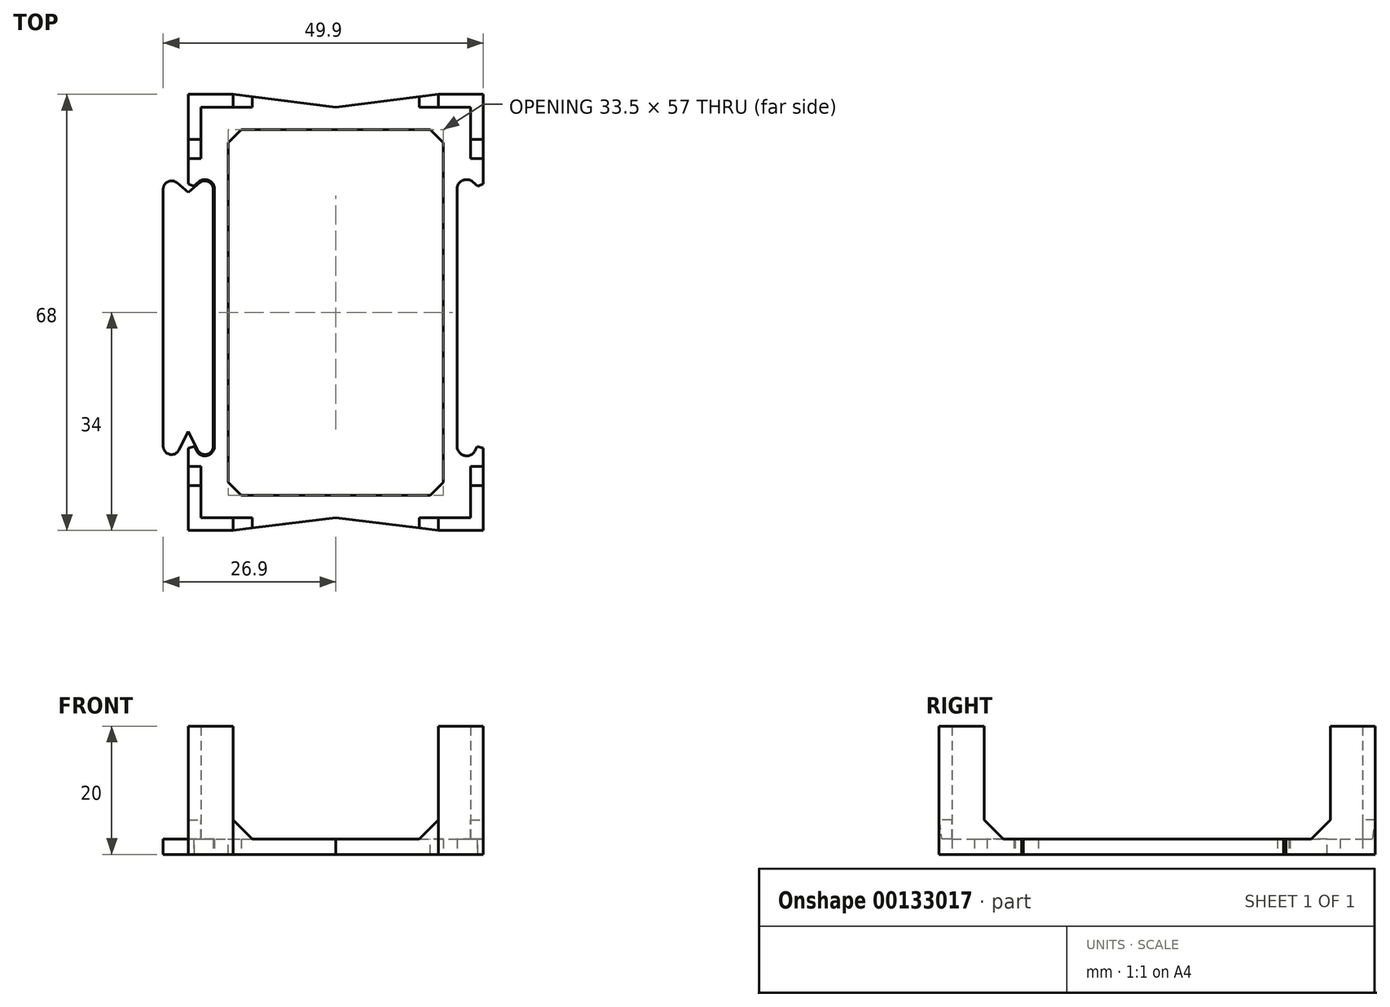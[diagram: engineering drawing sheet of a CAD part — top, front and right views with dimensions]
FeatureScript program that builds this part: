
annotation { "Feature Type Name" : "Feature", "Feature Type Description" : "" }
export const myFeature = defineFeature(function(context is Context, id is Id, definition is map)
    precondition{}
    {
        {
            var Q0;
            Q0=qCreatedBy(makeId("Top.planeOp"),FACE);
            var sketch = newSketch(context, id + "F0", { "sketchPlane" : qUnion([Q0])});
            skLineSegment(sketch, "E0.bottom", {"start": v(21, 32) * mm, "end": v(16, 32) * mm});
            skLineSegment(sketch, "E0.top", {"start": v(21, -32) * mm, "end": v(16, -32) * mm});
            skLineSegment(sketch, "E0.left", {"start": v(21, 32) * mm, "end": v(21, 27) * mm});
            skLineSegment(sketch, "E0.right", {"start": v(-21, 32) * mm, "end": v(-21, 27) * mm});
            skLineSegment(sketch, "E1", {"start": v(-16, 34) * mm, "end": v(-23, 34) * mm});
            skLineSegment(sketch, "E2", {"start": v(-23, 34) * mm, "end": v(-23, 27) * mm});
            skLineSegment(sketch, "E3", {"start": v(-16, 32) * mm, "end": v(-16, 34) * mm});
            skLineSegment(sketch, "E4", {"start": v(-21, 27) * mm, "end": v(-23, 27) * mm});
            skLineSegment(sketch, "E5", {"start": v(16, 34) * mm, "end": v(16, 32) * mm});
            skLineSegment(sketch, "E6", {"start": v(16, 34) * mm, "end": v(23, 34) * mm});
            skLineSegment(sketch, "E7", {"start": v(23, 27) * mm, "end": v(23, 34) * mm});
            skLineSegment(sketch, "E8", {"start": v(21, 27) * mm, "end": v(23, 27) * mm});
            skLineSegment(sketch, "E9", {"start": v(-23, -27) * mm, "end": v(-21, -27) * mm});
            skLineSegment(sketch, "E10", {"start": v(-23, -27) * mm, "end": v(-23, -34) * mm});
            skLineSegment(sketch, "E11", {"start": v(-16, -34) * mm, "end": v(-23, -34) * mm});
            skLineSegment(sketch, "E12", {"start": v(-16, -32) * mm, "end": v(-16, -34) * mm});
            skLineSegment(sketch, "E13", {"start": v(16, -32) * mm, "end": v(16, -34) * mm});
            skLineSegment(sketch, "E14", {"start": v(16, -34) * mm, "end": v(23, -34) * mm});
            skLineSegment(sketch, "E15", {"start": v(23, -27) * mm, "end": v(23, -34) * mm});
            skLineSegment(sketch, "E16", {"start": v(21, -27) * mm, "end": v(23, -27) * mm});
            skLineSegment(sketch, "E17", {"start": v(-16.75, 28.5) * mm, "end": v(16.75, 28.5) * mm});
            skLineSegment(sketch, "E18", {"start": v(16.75, -28.5) * mm, "end": v(-16.75, -28.5) * mm});
            skLineSegment(sketch, "E19", {"start": v(-16.75, 28.5) * mm, "end": v(-16.75, -28.5) * mm});
            skLineSegment(sketch, "E20", {"start": v(16.75, 28.5) * mm, "end": v(16.75, -28.5) * mm});
            skLineSegment(sketch, "E21", {"start": v(-16, 34) * mm, "end": v(0, 32) * mm});
            skLineSegment(sketch, "E22", {"start": v(0, 32) * mm, "end": v(16, 34) * mm});
            skLineSegment(sketch, "E23", {"start": v(-16, -34) * mm, "end": v(0, -32) * mm});
            skLineSegment(sketch, "E24", {"start": v(0, -32) * mm, "end": v(16, -34) * mm});
            skLineSegment(sketch, "E25.trimOffspring", {"start": v(21, -27) * mm, "end": v(21, -32) * mm});
            skLineSegment(sketch, "E26.trimOffspring", {"start": v(-16, -32) * mm, "end": v(-21, -32) * mm});
            skLineSegment(sketch, "E27.trimOffspring", {"start": v(-21, -27) * mm, "end": v(-21, -32) * mm});
            skLineSegment(sketch, "E28", {"start": v(-16, 32) * mm, "end": v(-21, 32) * mm});
            skPoint(sketch, "E29", {"position": v(0, 28.5) * mm});
            skPoint(sketch, "E30", {"position": v(0, -28.5) * mm});
            skPoint(sketch, "E31", {"position": v(-16.75, 0) * mm});
            skPoint(sketch, "E32", {"position": v(16.75, 0) * mm});
            skLineSegment(sketch, "E33", {"start": v(-23, 27) * mm, "end": v(-23, -27) * mm});
            skLineSegment(sketch, "E34", {"start": v(23, -27) * mm, "end": v(23, 27) * mm});
            skLineSegment(sketch, "E35", {"start": v(-23, 19) * mm, "end": v(-21.36, 20.37) * mm});
            skLineSegment(sketch, "E36", {"start": v(-18.9, 19.22) * mm, "end": v(-18.9, -20.86) * mm});
            skLineSegment(sketch, "E37", {"start": v(-21.74, -21.53) * mm, "end": v(-23, -19) * mm});
            skPoint(sketch, "E38.visualSharp", {"position": v(-18.9, 22.44) * mm});
            skArc(sketch, "E38.filletArc", {"start": v(-18.9, 19.22) * mm, "mid": v(-19.76, 20.58) * mm, "end": v(-21.36, 20.37) * mm});
            skPoint(sketch, "E39.visualSharp", {"position": v(-18.9, -27.23) * mm});
            skArc(sketch, "E39.filletArc", {"start": v(-21.74, -21.53) * mm, "mid": v(-20.06, -22.32) * mm, "end": v(-18.9, -20.86) * mm});
            skLineSegment(sketch, "E40.MirrorCS", {"start": v(-23, 19) * mm, "end": v(-24.64, 20.37) * mm});
            skArc(sketch, "E41.MirrorCS", {"start": v(-27.1, 19.22) * mm, "mid": v(-26.24, 20.58) * mm, "end": v(-24.64, 20.37) * mm});
            skLineSegment(sketch, "E42.MirrorCS", {"start": v(-27.1, 19.22) * mm, "end": v(-27.1, -20.86) * mm});
            skArc(sketch, "E43.MirrorCS", {"start": v(-24.26, -21.53) * mm, "mid": v(-25.94, -22.32) * mm, "end": v(-27.1, -20.86) * mm});
            skLineSegment(sketch, "E44.MirrorCS", {"start": v(-24.26, -21.53) * mm, "end": v(-23, -19) * mm});
            skLineSegment(sketch, "E45", {"start": v(0, 40.79) * mm, "end": v(0, -39.35) * mm, "construction": true});
            skLineSegment(sketch, "E46.MirrorCS", {"start": v(18.9, 19.22) * mm, "end": v(18.9, -20.86) * mm});
            skArc(sketch, "E47.MirrorCS", {"start": v(18.9, 19.22) * mm, "mid": v(19.76, 20.58) * mm, "end": v(21.36, 20.37) * mm});
            skLineSegment(sketch, "E48.MirrorCS", {"start": v(23, 19) * mm, "end": v(21.36, 20.37) * mm});
            skLineSegment(sketch, "E49.MirrorCS", {"start": v(23, 19) * mm, "end": v(24.64, 20.37) * mm});
            skArc(sketch, "E50.MirrorCS", {"start": v(27.1, 19.22) * mm, "mid": v(26.24, 20.58) * mm, "end": v(24.64, 20.37) * mm});
            skLineSegment(sketch, "E51.MirrorCS", {"start": v(27.1, 19.22) * mm, "end": v(27.1, -20.86) * mm});
            skArc(sketch, "E52.MirrorCS", {"start": v(24.26, -21.53) * mm, "mid": v(25.94, -22.32) * mm, "end": v(27.1, -20.86) * mm});
            skLineSegment(sketch, "E53.MirrorCS", {"start": v(24.26, -21.53) * mm, "end": v(23, -19) * mm});
            skLineSegment(sketch, "E54.MirrorCS", {"start": v(21.74, -21.53) * mm, "end": v(23, -19) * mm});
            skArc(sketch, "E55.MirrorCS", {"start": v(21.74, -21.53) * mm, "mid": v(20.06, -22.32) * mm, "end": v(18.9, -20.86) * mm});
            skArc(sketch, "E56.0", {"start": v(-19.1, 19.22) * mm, "mid": v(-19.85, 20.4) * mm, "end": v(-21.23, 20.22) * mm});
            skLineSegment(sketch, "E56.1", {"start": v(-23, 18.74) * mm, "end": v(-21.23, 20.22) * mm});
            skLineSegment(sketch, "E56.2", {"start": v(-19.1, 19.22) * mm, "end": v(-19.1, -20.86) * mm});
            skLineSegment(sketch, "E56.3", {"start": v(-23, 18.74) * mm, "end": v(-24.77, 20.22) * mm});
            skArc(sketch, "E56.4", {"start": v(-26.9, 19.22) * mm, "mid": v(-26.15, 20.4) * mm, "end": v(-24.77, 20.22) * mm});
            skLineSegment(sketch, "E56.5", {"start": v(-26.9, 19.22) * mm, "end": v(-26.9, -20.86) * mm});
            skArc(sketch, "E56.6", {"start": v(-21.56, -21.44) * mm, "mid": v(-20.1, -22.12) * mm, "end": v(-19.1, -20.86) * mm});
            skLineSegment(sketch, "E56.7", {"start": v(-21.56, -21.44) * mm, "end": v(-23, -18.55) * mm});
            skLineSegment(sketch, "E56.8", {"start": v(-24.44, -21.44) * mm, "end": v(-23, -18.55) * mm});
            skArc(sketch, "E56.9", {"start": v(-24.44, -21.44) * mm, "mid": v(-25.9, -22.12) * mm, "end": v(-26.9, -20.86) * mm});
            skLineSegment(sketch, "E57.0", {"start": v(-23.9, 19.22) * mm, "end": v(-23.9, -20.86) * mm});
            skSolve(sketch);
        }
        {
            var Q0;
            {var subQ0=sQuery(id+"F0.wireOp",EDGE,"E0.left");var subQ3=sQuery(id+"F0.wireOp",EDGE,"E0.bottom");var subQ4=makeQuery(id+"F0.imprint","INTERSECT",VERTEX,{"derivedFrom":[subQ3,subQ0]});Q0=makeQuery(id+"F0.imprint","IMPRINT",FACE,{"disambiguationData":[TD([[makeQuery(id+"F0.imprint","IMPRINT",EDGE,{"disambiguationData":[TD([[subQ4,-1.0]])],"derivedFrom":subQ3}),1.0]])]});}
            var Q1;
            {var subQ0=sQuery(id+"F0.wireOp",EDGE,"E5");Q1=makeQuery(id+"F0.imprint","IMPRINT",FACE,{"disambiguationData":[TD([[makeQuery(id+"F0.imprint","IMPRINT",EDGE,{"derivedFrom":subQ0}),-1.0]])]});}
            var Q2;
            {var subQ4=sQuery(id+"F0.wireOp",EDGE,"E5");Q2=makeQuery(id+"F0.imprint","IMPRINT",FACE,{"disambiguationData":[TD([[makeQuery(id+"F0.imprint","IMPRINT",EDGE,{"derivedFrom":subQ4}),1.0]])]});}
            var Q3;
            {var subQ0=sQuery(id+"F0.wireOp",EDGE,"E8");Q3=makeQuery(id+"F0.imprint","IMPRINT",FACE,{"disambiguationData":[TD([[makeQuery(id+"F0.imprint","IMPRINT",EDGE,{"derivedFrom":subQ0}),-1.0]])]});}
            var Q4;
            {var subQ0=sQuery(id+"F0.wireOp",EDGE,"E16");Q4=makeQuery(id+"F0.imprint","IMPRINT",FACE,{"disambiguationData":[TD([[makeQuery(id+"F0.imprint","IMPRINT",EDGE,{"derivedFrom":subQ0}),1.0]])]});}
            var Q5;
            {var subQ0=sQuery(id+"F0.wireOp",EDGE,"E13");Q5=makeQuery(id+"F0.imprint","IMPRINT",FACE,{"disambiguationData":[TD([[makeQuery(id+"F0.imprint","IMPRINT",EDGE,{"derivedFrom":subQ0}),1.0]])]});}
            var Q6;
            {var subQ0=sQuery(id+"F0.wireOp",EDGE,"E13");Q6=makeQuery(id+"F0.imprint","IMPRINT",FACE,{"disambiguationData":[TD([[makeQuery(id+"F0.imprint","IMPRINT",EDGE,{"derivedFrom":subQ0}),-1.0]])]});}
            var Q7;
            {var subQ0=sQuery(id+"F0.wireOp",EDGE,"E12");Q7=makeQuery(id+"F0.imprint","IMPRINT",FACE,{"disambiguationData":[TD([[makeQuery(id+"F0.imprint","IMPRINT",EDGE,{"derivedFrom":subQ0}),1.0]])]});}
            var Q8;
            {var subQ4=sQuery(id+"F0.wireOp",EDGE,"E9");Q8=makeQuery(id+"F0.imprint","IMPRINT",FACE,{"disambiguationData":[TD([[makeQuery(id+"F0.imprint","IMPRINT",EDGE,{"derivedFrom":subQ4}),-1.0]])]});}
            var Q9;
            {var subQ0=sQuery(id+"F0.wireOp",EDGE,"E9");Q9=makeQuery(id+"F0.imprint","IMPRINT",FACE,{"disambiguationData":[TD([[makeQuery(id+"F0.imprint","IMPRINT",EDGE,{"derivedFrom":subQ0}),1.0]])]});}
            var Q10;
            {var subQ0=sQuery(id+"F0.wireOp",EDGE,"E4");Q10=makeQuery(id+"F0.imprint","IMPRINT",FACE,{"disambiguationData":[TD([[makeQuery(id+"F0.imprint","IMPRINT",EDGE,{"derivedFrom":subQ0}),1.0]])]});}
            var Q11;
            Q11=makeQuery(id+"F0.imprint","IMPRINT",FACE,{"disambiguationData":[TD([[makeQuery(id+"F0.imprint","IMPRINT",EDGE,{"derivedFrom":sQuery(id+"F0.wireOp",EDGE,"E1")}),1.0]])]});
            var Q12;
            {var subQ0=sQuery(id+"F0.wireOp",EDGE,"E3");Q12=makeQuery(id+"F0.imprint","IMPRINT",FACE,{"disambiguationData":[TD([[makeQuery(id+"F0.imprint","IMPRINT",EDGE,{"derivedFrom":subQ0}),-1.0]])]});}
            extrude(context, id + "F1", {"entities" : qUnion([Q0, Q1, Q2, Q3, Q4, Q5, Q6, Q7, Q8, Q9, Q10, Q11, Q12]), "depth" : 2.4 * mm});
        }
        {
            var Q0;
            Q0=makeQuery(id+"F0.imprint","IMPRINT",FACE,{"disambiguationData":[TD([[makeQuery(id+"F0.imprint","IMPRINT",EDGE,{"derivedFrom":sQuery(id+"F0.wireOp",EDGE,"E1")}),1.0]])]});
            var Q1;
            {var subQ4=sQuery(id+"F0.wireOp",EDGE,"E5");Q1=makeQuery(id+"F0.imprint","IMPRINT",FACE,{"disambiguationData":[TD([[makeQuery(id+"F0.imprint","IMPRINT",EDGE,{"derivedFrom":subQ4}),1.0]])]});}
            var Q2;
            {var subQ0=sQuery(id+"F0.wireOp",EDGE,"E13");Q2=makeQuery(id+"F0.imprint","IMPRINT",FACE,{"disambiguationData":[TD([[makeQuery(id+"F0.imprint","IMPRINT",EDGE,{"derivedFrom":subQ0}),1.0]])]});}
            var Q3;
            {var subQ3=sQuery(id+"F0.wireOp",EDGE,"E9");Q3=makeQuery(id+"F0.imprint","IMPRINT",FACE,{"disambiguationData":[TD([[makeQuery(id+"F0.imprint","IMPRINT",EDGE,{"derivedFrom":subQ3}),-1.0]])]});}
            extrude(context, id + "F2", {"entities" : qUnion([Q0, Q1, Q2, Q3]), "operationType" : NewBodyOperationType.ADD, "depth" : 20 * mm});
        }
        {
            var Q0;
            Q0=makeQuery(id+"F2.boolean.opBoolean","INTERSECT",EDGE,{"derivedFrom":[makeQuery(id+"F1.opExtrude","CAP_FACE",FACE,{"disambiguationData":[OSD([sQuery(id+"F0.wireOp",EDGE,"E1"),sQuery(id+"F0.wireOp",EDGE,"E2"),sQuery(id+"F0.wireOp",EDGE,"E6"),sQuery(id+"F0.wireOp",EDGE,"E7"),sQuery(id+"F0.wireOp",EDGE,"E10"),sQuery(id+"F0.wireOp",EDGE,"E11"),sQuery(id+"F0.wireOp",EDGE,"E14"),sQuery(id+"F0.wireOp",EDGE,"E15"),sQuery(id+"F0.wireOp",EDGE,"E17"),sQuery(id+"F0.wireOp",EDGE,"E18"),sQuery(id+"F0.wireOp",EDGE,"E19"),sQuery(id+"F0.wireOp",EDGE,"E20"),sQuery(id+"F0.wireOp",EDGE,"jiaWZDtS-R24L-EVNI-qtd6-zTstN88FOwR1"),sQuery(id+"F0.wireOp",EDGE,"sGljjnvT-gn0O-4xuL-FiDi-xVXoTiZH4aIa"),sQuery(id+"F0.wireOp",EDGE,"JoJTnnvT-VXK7-kJcO-3MJ3-lJnIAB2w7SyZ"),sQuery(id+"F0.wireOp",EDGE,"D99VeNCh-oXrI-DHgS-fi0i-UPG9c3mJZdQb"),sQuery(id+"F0.wireOp",EDGE,"E21"),sQuery(id+"F0.wireOp",EDGE,"E22"),sQuery(id+"F0.wireOp",EDGE,"E23"),sQuery(id+"F0.wireOp",EDGE,"E24")])],"isStart":false}),makeQuery(id+"F2.opExtrude","SWEPT_FACE",FACE,{"disambiguationData":[OSD([sQuery(id+"F0.wireOp",EDGE,"E4")])]})]});
            var Q1;
            Q1=makeQuery(id+"F2.boolean.opBoolean","INTERSECT",EDGE,{"derivedFrom":[makeQuery(id+"F1.opExtrude","CAP_FACE",FACE,{"disambiguationData":[OSD([sQuery(id+"F0.wireOp",EDGE,"E1"),sQuery(id+"F0.wireOp",EDGE,"E2"),sQuery(id+"F0.wireOp",EDGE,"E6"),sQuery(id+"F0.wireOp",EDGE,"E7"),sQuery(id+"F0.wireOp",EDGE,"E10"),sQuery(id+"F0.wireOp",EDGE,"E11"),sQuery(id+"F0.wireOp",EDGE,"E14"),sQuery(id+"F0.wireOp",EDGE,"E15"),sQuery(id+"F0.wireOp",EDGE,"E17"),sQuery(id+"F0.wireOp",EDGE,"E18"),sQuery(id+"F0.wireOp",EDGE,"E19"),sQuery(id+"F0.wireOp",EDGE,"E20"),sQuery(id+"F0.wireOp",EDGE,"jiaWZDtS-R24L-EVNI-qtd6-zTstN88FOwR1"),sQuery(id+"F0.wireOp",EDGE,"sGljjnvT-gn0O-4xuL-FiDi-xVXoTiZH4aIa"),sQuery(id+"F0.wireOp",EDGE,"JoJTnnvT-VXK7-kJcO-3MJ3-lJnIAB2w7SyZ"),sQuery(id+"F0.wireOp",EDGE,"D99VeNCh-oXrI-DHgS-fi0i-UPG9c3mJZdQb"),sQuery(id+"F0.wireOp",EDGE,"E21"),sQuery(id+"F0.wireOp",EDGE,"E22"),sQuery(id+"F0.wireOp",EDGE,"E23"),sQuery(id+"F0.wireOp",EDGE,"E24")])],"isStart":false}),makeQuery(id+"F2.opExtrude","SWEPT_FACE",FACE,{"disambiguationData":[OSD([sQuery(id+"F0.wireOp",EDGE,"E3")])]})]});
            var Q2;
            Q2=makeQuery(id+"F2.boolean.opBoolean","INTERSECT",EDGE,{"derivedFrom":[makeQuery(id+"F1.opExtrude","CAP_FACE",FACE,{"disambiguationData":[OSD([sQuery(id+"F0.wireOp",EDGE,"E1"),sQuery(id+"F0.wireOp",EDGE,"E2"),sQuery(id+"F0.wireOp",EDGE,"E6"),sQuery(id+"F0.wireOp",EDGE,"E7"),sQuery(id+"F0.wireOp",EDGE,"E10"),sQuery(id+"F0.wireOp",EDGE,"E11"),sQuery(id+"F0.wireOp",EDGE,"E14"),sQuery(id+"F0.wireOp",EDGE,"E15"),sQuery(id+"F0.wireOp",EDGE,"E17"),sQuery(id+"F0.wireOp",EDGE,"E18"),sQuery(id+"F0.wireOp",EDGE,"E19"),sQuery(id+"F0.wireOp",EDGE,"E20"),sQuery(id+"F0.wireOp",EDGE,"jiaWZDtS-R24L-EVNI-qtd6-zTstN88FOwR1"),sQuery(id+"F0.wireOp",EDGE,"sGljjnvT-gn0O-4xuL-FiDi-xVXoTiZH4aIa"),sQuery(id+"F0.wireOp",EDGE,"JoJTnnvT-VXK7-kJcO-3MJ3-lJnIAB2w7SyZ"),sQuery(id+"F0.wireOp",EDGE,"D99VeNCh-oXrI-DHgS-fi0i-UPG9c3mJZdQb"),sQuery(id+"F0.wireOp",EDGE,"E21"),sQuery(id+"F0.wireOp",EDGE,"E22"),sQuery(id+"F0.wireOp",EDGE,"E23"),sQuery(id+"F0.wireOp",EDGE,"E24")])],"isStart":false}),makeQuery(id+"F2.opExtrude","SWEPT_FACE",FACE,{"disambiguationData":[OSD([sQuery(id+"F0.wireOp",EDGE,"E8")])]})]});
            var Q3;
            Q3=makeQuery(id+"F2.boolean.opBoolean","INTERSECT",EDGE,{"derivedFrom":[makeQuery(id+"F1.opExtrude","CAP_FACE",FACE,{"disambiguationData":[OSD([sQuery(id+"F0.wireOp",EDGE,"E1"),sQuery(id+"F0.wireOp",EDGE,"E2"),sQuery(id+"F0.wireOp",EDGE,"E6"),sQuery(id+"F0.wireOp",EDGE,"E7"),sQuery(id+"F0.wireOp",EDGE,"E10"),sQuery(id+"F0.wireOp",EDGE,"E11"),sQuery(id+"F0.wireOp",EDGE,"E14"),sQuery(id+"F0.wireOp",EDGE,"E15"),sQuery(id+"F0.wireOp",EDGE,"E17"),sQuery(id+"F0.wireOp",EDGE,"E18"),sQuery(id+"F0.wireOp",EDGE,"E19"),sQuery(id+"F0.wireOp",EDGE,"E20"),sQuery(id+"F0.wireOp",EDGE,"jiaWZDtS-R24L-EVNI-qtd6-zTstN88FOwR1"),sQuery(id+"F0.wireOp",EDGE,"sGljjnvT-gn0O-4xuL-FiDi-xVXoTiZH4aIa"),sQuery(id+"F0.wireOp",EDGE,"JoJTnnvT-VXK7-kJcO-3MJ3-lJnIAB2w7SyZ"),sQuery(id+"F0.wireOp",EDGE,"D99VeNCh-oXrI-DHgS-fi0i-UPG9c3mJZdQb"),sQuery(id+"F0.wireOp",EDGE,"E21"),sQuery(id+"F0.wireOp",EDGE,"E22"),sQuery(id+"F0.wireOp",EDGE,"E23"),sQuery(id+"F0.wireOp",EDGE,"E24")])],"isStart":false}),makeQuery(id+"F2.opExtrude","SWEPT_FACE",FACE,{"disambiguationData":[OSD([sQuery(id+"F0.wireOp",EDGE,"E5")])]})]});
            var Q4;
            Q4=makeQuery(id+"F2.boolean.opBoolean","INTERSECT",EDGE,{"derivedFrom":[makeQuery(id+"F1.opExtrude","CAP_FACE",FACE,{"disambiguationData":[OSD([sQuery(id+"F0.wireOp",EDGE,"E1"),sQuery(id+"F0.wireOp",EDGE,"E2"),sQuery(id+"F0.wireOp",EDGE,"E6"),sQuery(id+"F0.wireOp",EDGE,"E7"),sQuery(id+"F0.wireOp",EDGE,"E10"),sQuery(id+"F0.wireOp",EDGE,"E11"),sQuery(id+"F0.wireOp",EDGE,"E14"),sQuery(id+"F0.wireOp",EDGE,"E15"),sQuery(id+"F0.wireOp",EDGE,"E17"),sQuery(id+"F0.wireOp",EDGE,"E18"),sQuery(id+"F0.wireOp",EDGE,"E19"),sQuery(id+"F0.wireOp",EDGE,"E20"),sQuery(id+"F0.wireOp",EDGE,"jiaWZDtS-R24L-EVNI-qtd6-zTstN88FOwR1"),sQuery(id+"F0.wireOp",EDGE,"sGljjnvT-gn0O-4xuL-FiDi-xVXoTiZH4aIa"),sQuery(id+"F0.wireOp",EDGE,"JoJTnnvT-VXK7-kJcO-3MJ3-lJnIAB2w7SyZ"),sQuery(id+"F0.wireOp",EDGE,"D99VeNCh-oXrI-DHgS-fi0i-UPG9c3mJZdQb"),sQuery(id+"F0.wireOp",EDGE,"E21"),sQuery(id+"F0.wireOp",EDGE,"E22"),sQuery(id+"F0.wireOp",EDGE,"E23"),sQuery(id+"F0.wireOp",EDGE,"E24")])],"isStart":false}),makeQuery(id+"F2.opExtrude","SWEPT_FACE",FACE,{"disambiguationData":[OSD([sQuery(id+"F0.wireOp",EDGE,"E12")])]})]});
            var Q5;
            Q5=makeQuery(id+"F2.boolean.opBoolean","INTERSECT",EDGE,{"derivedFrom":[makeQuery(id+"F1.opExtrude","CAP_FACE",FACE,{"disambiguationData":[OSD([sQuery(id+"F0.wireOp",EDGE,"E1"),sQuery(id+"F0.wireOp",EDGE,"E2"),sQuery(id+"F0.wireOp",EDGE,"E6"),sQuery(id+"F0.wireOp",EDGE,"E7"),sQuery(id+"F0.wireOp",EDGE,"E10"),sQuery(id+"F0.wireOp",EDGE,"E11"),sQuery(id+"F0.wireOp",EDGE,"E14"),sQuery(id+"F0.wireOp",EDGE,"E15"),sQuery(id+"F0.wireOp",EDGE,"E17"),sQuery(id+"F0.wireOp",EDGE,"E18"),sQuery(id+"F0.wireOp",EDGE,"E19"),sQuery(id+"F0.wireOp",EDGE,"E20"),sQuery(id+"F0.wireOp",EDGE,"jiaWZDtS-R24L-EVNI-qtd6-zTstN88FOwR1"),sQuery(id+"F0.wireOp",EDGE,"sGljjnvT-gn0O-4xuL-FiDi-xVXoTiZH4aIa"),sQuery(id+"F0.wireOp",EDGE,"JoJTnnvT-VXK7-kJcO-3MJ3-lJnIAB2w7SyZ"),sQuery(id+"F0.wireOp",EDGE,"D99VeNCh-oXrI-DHgS-fi0i-UPG9c3mJZdQb"),sQuery(id+"F0.wireOp",EDGE,"E21"),sQuery(id+"F0.wireOp",EDGE,"E22"),sQuery(id+"F0.wireOp",EDGE,"E23"),sQuery(id+"F0.wireOp",EDGE,"E24")])],"isStart":false}),makeQuery(id+"F2.opExtrude","SWEPT_FACE",FACE,{"disambiguationData":[OSD([sQuery(id+"F0.wireOp",EDGE,"E9")])]})]});
            var Q6;
            Q6=makeQuery(id+"F2.boolean.opBoolean","INTERSECT",EDGE,{"derivedFrom":[makeQuery(id+"F1.opExtrude","CAP_FACE",FACE,{"disambiguationData":[OSD([sQuery(id+"F0.wireOp",EDGE,"E1"),sQuery(id+"F0.wireOp",EDGE,"E2"),sQuery(id+"F0.wireOp",EDGE,"E6"),sQuery(id+"F0.wireOp",EDGE,"E7"),sQuery(id+"F0.wireOp",EDGE,"E10"),sQuery(id+"F0.wireOp",EDGE,"E11"),sQuery(id+"F0.wireOp",EDGE,"E14"),sQuery(id+"F0.wireOp",EDGE,"E15"),sQuery(id+"F0.wireOp",EDGE,"E17"),sQuery(id+"F0.wireOp",EDGE,"E18"),sQuery(id+"F0.wireOp",EDGE,"E19"),sQuery(id+"F0.wireOp",EDGE,"E20"),sQuery(id+"F0.wireOp",EDGE,"jiaWZDtS-R24L-EVNI-qtd6-zTstN88FOwR1"),sQuery(id+"F0.wireOp",EDGE,"sGljjnvT-gn0O-4xuL-FiDi-xVXoTiZH4aIa"),sQuery(id+"F0.wireOp",EDGE,"JoJTnnvT-VXK7-kJcO-3MJ3-lJnIAB2w7SyZ"),sQuery(id+"F0.wireOp",EDGE,"D99VeNCh-oXrI-DHgS-fi0i-UPG9c3mJZdQb"),sQuery(id+"F0.wireOp",EDGE,"E21"),sQuery(id+"F0.wireOp",EDGE,"E22"),sQuery(id+"F0.wireOp",EDGE,"E23"),sQuery(id+"F0.wireOp",EDGE,"E24")])],"isStart":false}),makeQuery(id+"F2.opExtrude","SWEPT_FACE",FACE,{"disambiguationData":[OSD([sQuery(id+"F0.wireOp",EDGE,"E16")])]})]});
            var Q7;
            Q7=makeQuery(id+"F2.boolean.opBoolean","INTERSECT",EDGE,{"derivedFrom":[makeQuery(id+"F1.opExtrude","CAP_FACE",FACE,{"disambiguationData":[OSD([sQuery(id+"F0.wireOp",EDGE,"E1"),sQuery(id+"F0.wireOp",EDGE,"E2"),sQuery(id+"F0.wireOp",EDGE,"E6"),sQuery(id+"F0.wireOp",EDGE,"E7"),sQuery(id+"F0.wireOp",EDGE,"E10"),sQuery(id+"F0.wireOp",EDGE,"E11"),sQuery(id+"F0.wireOp",EDGE,"E14"),sQuery(id+"F0.wireOp",EDGE,"E15"),sQuery(id+"F0.wireOp",EDGE,"E17"),sQuery(id+"F0.wireOp",EDGE,"E18"),sQuery(id+"F0.wireOp",EDGE,"E19"),sQuery(id+"F0.wireOp",EDGE,"E20"),sQuery(id+"F0.wireOp",EDGE,"jiaWZDtS-R24L-EVNI-qtd6-zTstN88FOwR1"),sQuery(id+"F0.wireOp",EDGE,"sGljjnvT-gn0O-4xuL-FiDi-xVXoTiZH4aIa"),sQuery(id+"F0.wireOp",EDGE,"JoJTnnvT-VXK7-kJcO-3MJ3-lJnIAB2w7SyZ"),sQuery(id+"F0.wireOp",EDGE,"D99VeNCh-oXrI-DHgS-fi0i-UPG9c3mJZdQb"),sQuery(id+"F0.wireOp",EDGE,"E21"),sQuery(id+"F0.wireOp",EDGE,"E22"),sQuery(id+"F0.wireOp",EDGE,"E23"),sQuery(id+"F0.wireOp",EDGE,"E24")])],"isStart":false}),makeQuery(id+"F2.opExtrude","SWEPT_FACE",FACE,{"disambiguationData":[OSD([sQuery(id+"F0.wireOp",EDGE,"E13")])]})]});
            chamfer(context, id + "F3", {"entities" : qUnion([Q0, Q1, Q2, Q3, Q4, Q5, Q6, Q7]), "width" : 3 * mm, "tangentPropagation" : true});
        }
        {
            var Q0;
            Q0=makeQuery(id+"F1.opExtrude","SWEPT_EDGE",EDGE,{"disambiguationData":[OSD([sQuery(id+"F0.wireOp",EDGE,"E17"),sQuery(id+"F0.wireOp",EDGE,"E19")])]});
            var Q1;
            Q1=makeQuery(id+"F1.opExtrude","SWEPT_EDGE",EDGE,{"disambiguationData":[OSD([sQuery(id+"F0.wireOp",EDGE,"E17"),sQuery(id+"F0.wireOp",EDGE,"E20")])]});
            var Q2;
            Q2=makeQuery(id+"F1.opExtrude","SWEPT_EDGE",EDGE,{"disambiguationData":[OSD([sQuery(id+"F0.wireOp",EDGE,"E18"),sQuery(id+"F0.wireOp",EDGE,"E19")])]});
            var Q3;
            Q3=makeQuery(id+"F1.opExtrude","SWEPT_EDGE",EDGE,{"disambiguationData":[OSD([sQuery(id+"F0.wireOp",EDGE,"E18"),sQuery(id+"F0.wireOp",EDGE,"E20")])]});
            chamfer(context, id + "F4", {"entities" : qUnion([Q0, Q1, Q2, Q3]), "width" : 2 * mm, "tangentPropagation" : true});
        }
        {
            var Q0;
            Q0=makeQuery(id+"F0.imprint","IMPRINT",FACE,{"disambiguationData":[TD([[makeQuery(id+"F0.imprint","IMPRINT",EDGE,{"derivedFrom":sQuery(id+"F0.wireOp",EDGE,"E56.0")}),1.0]])]});
            var Q1;
            {var subQ0=sQuery(id+"F0.wireOp",EDGE,"E56.3");Q1=makeQuery(id+"F0.imprint","IMPRINT",FACE,{"disambiguationData":[TD([[makeQuery(id+"F0.imprint","IMPRINT",EDGE,{"derivedFrom":subQ0}),1.0]])]});}
            extrude(context, id + "F5", {"entities" : qUnion([Q0, Q1]), "depth" : 2.4 * mm});
        }
        {
            var Q0;
            Q0=makeQuery(id+"F1.opExtrude","SWEPT_EDGE",EDGE,{"disambiguationData":[OSD([sQuery(id+"F0.wireOp",EDGE,"E33"),sQuery(id+"F0.wireOp",EDGE,"E35"),sQuery(id+"F0.wireOp",EDGE,"E40.MirrorCS")])]});
            var Q1;
            Q1=makeQuery(id+"F1.opExtrude","SWEPT_EDGE",EDGE,{"disambiguationData":[OSD([sQuery(id+"F0.wireOp",EDGE,"E33"),sQuery(id+"F0.wireOp",EDGE,"E37"),sQuery(id+"F0.wireOp",EDGE,"E44.MirrorCS")])]});
            var Q2;
            Q2=makeQuery(id+"F1.opExtrude","SWEPT_EDGE",EDGE,{"disambiguationData":[OSD([sQuery(id+"F0.wireOp",EDGE,"E34"),sQuery(id+"F0.wireOp",EDGE,"E48.MirrorCS"),sQuery(id+"F0.wireOp",EDGE,"E49.MirrorCS")])]});
            var Q3;
            Q3=makeQuery(id+"F1.opExtrude","SWEPT_EDGE",EDGE,{"disambiguationData":[OSD([sQuery(id+"F0.wireOp",EDGE,"E34"),sQuery(id+"F0.wireOp",EDGE,"E53.MirrorCS"),sQuery(id+"F0.wireOp",EDGE,"E54.MirrorCS")])]});
            chamfer(context, id + "F6", {"entities" : qUnion([Q0, Q1, Q2, Q3]), "width" : .5 * mm, "tangentPropagation" : true});
        }
    });
